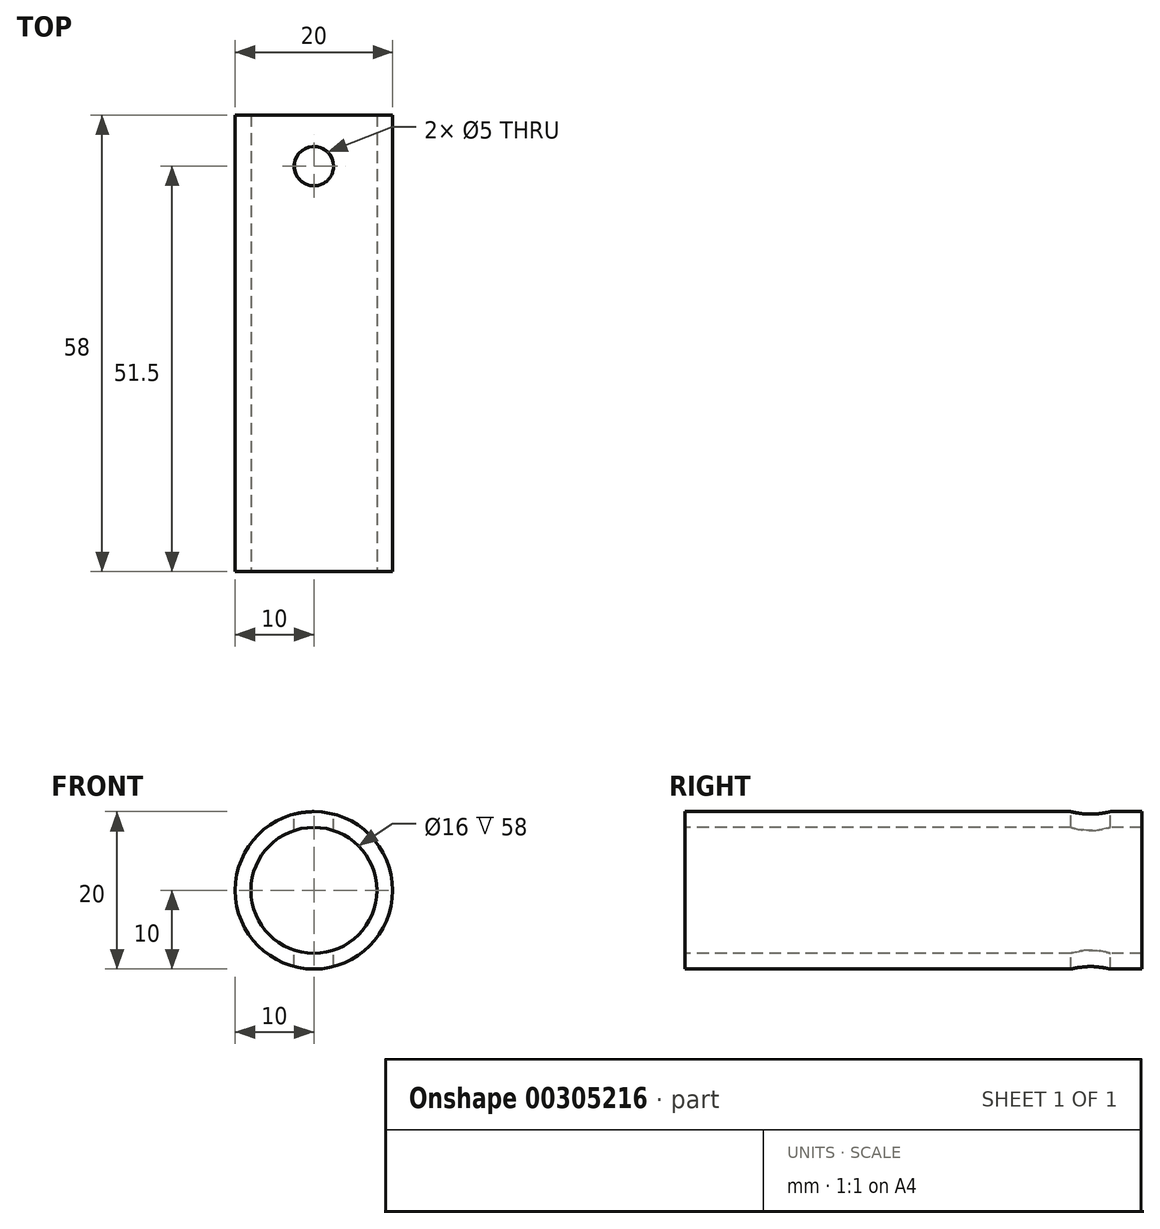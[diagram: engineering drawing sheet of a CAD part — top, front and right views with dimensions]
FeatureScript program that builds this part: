
annotation { "Feature Type Name" : "Feature", "Feature Type Description" : "" }
export const myFeature = defineFeature(function(context is Context, id is Id, definition is map)
    precondition{}
    {
        {
            var Q0;
            Q0=qCreatedBy(makeId("Front.planeOp"),FACE);
            var sketch = newSketch(context, id + "F0", { "sketchPlane" : qUnion([Q0])});
            skCircle(sketch, "E0", {"center": v(0, 0) * mm, "radius": 10 * mm});
            skSolve(sketch);
        }
        {
            var Q0;
            Q0=makeQuery(id+"F0.imprint","IMPRINT",FACE,{"disambiguationData":[TD([[makeQuery(id+"F0.imprint","IMPRINT",EDGE,{"derivedFrom":sQuery(id+"F0.wireOp",EDGE,"E0")}),1.0]])]});
            extrude(context, id + "F1", {"entities" : qUnion([Q0]), "depth" : 58 * mm});
        }
        {
            var Q0;
            Q0=makeQuery(id+"F1.opExtrude","CAP_FACE",FACE,{"disambiguationData":[OSD([sQuery(id+"F0.wireOp",EDGE,"E0")])],"isStart":false});
            var sketch = newSketch(context, id + "F2", { "sketchPlane" : qUnion([Q0])});
            skCircle(sketch, "E1", {"center": v(0, 0) * mm, "radius": 8 * mm});
            skSolve(sketch);
        }
        {
            var Q0;
            Q0=makeQuery(id+"F2.imprint","IMPRINT",FACE,{"disambiguationData":[TD([[makeQuery(id+"F2.imprint","IMPRINT",EDGE,{"derivedFrom":sQuery(id+"F2.wireOp",EDGE,"E1")}),1.0]])]});
            extrude(context, id + "F3", {"entities" : qUnion([Q0]), "operationType" : NewBodyOperationType.REMOVE, "oppositeDirection" : true, "depth" : 60 * mm});
        }
        {
            var Q0;
            Q0=qCreatedBy(makeId("Top.planeOp"),FACE);
            var sketch = newSketch(context, id + "F4", { "sketchPlane" : qUnion([Q0])});
            skCircle(sketch, "E2", {"center": v(0, -6.5) * mm, "radius": 2.5 * mm});
            skSolve(sketch);
        }
        {
            var Q0;
            Q0 = qSketchRegion(id + "F4", true);
            extrude(context, id + "F5", {"entities" : qUnion([Q0]), "operationType" : NewBodyOperationType.REMOVE, "oppositeDirection" : true, "depth" : 25 * mm, "hasSecondDirection" : true, "secondDirectionOppositeDirection" : false, "secondDirectionDepth" : 25 * mm});
        }
    });
